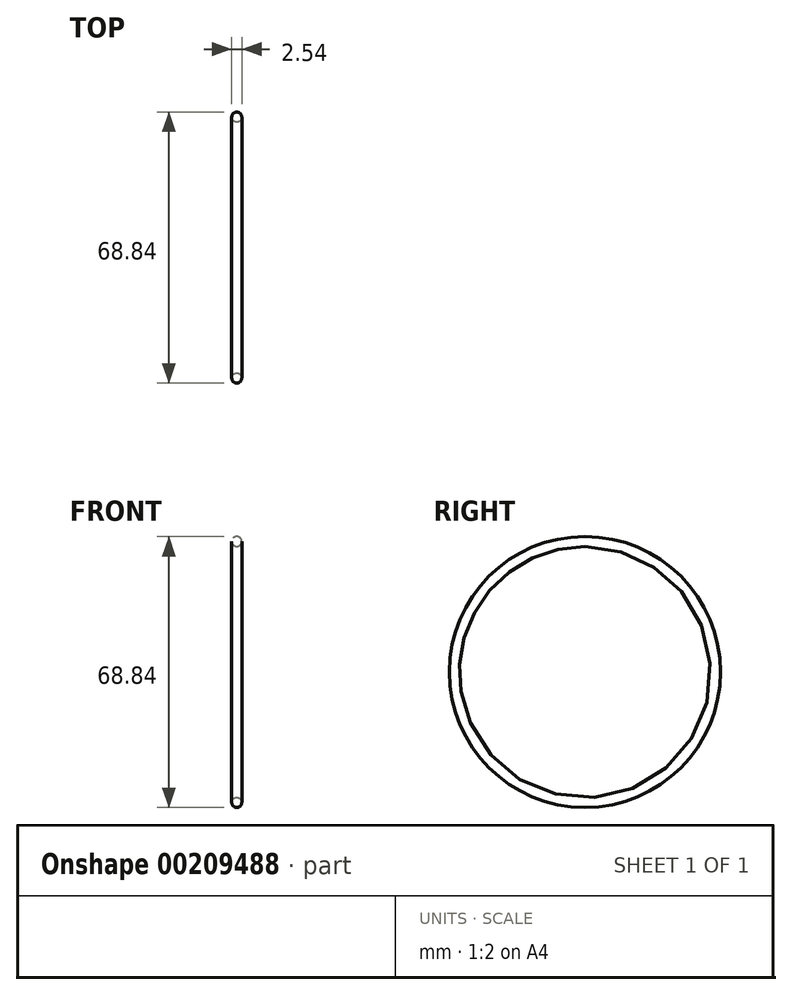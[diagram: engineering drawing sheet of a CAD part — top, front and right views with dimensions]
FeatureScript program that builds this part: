
annotation { "Feature Type Name" : "Feature", "Feature Type Description" : "" }
export const myFeature = defineFeature(function(context is Context, id is Id, definition is map)
    precondition{}
    {
        {
            var Q0;
            Q0=qCreatedBy(makeId("Front.planeOp"),FACE);
            var sketch = newSketch(context, id + "F0", { "sketchPlane" : qUnion([Q0])});
            skCircle(sketch, "E0", {"center": v(0, 33.15) * mm, "radius": 1.27 * mm});
            skLineSegment(sketch, "E1", {"start": v(-11.38, 0) * mm, "end": v(23.45, 0) * mm});
            skSolve(sketch);
        }
        {
            var Q0;
            Q0 = qSketchRegion(id + "F0", true);
            var Q1;
            Q1=sQuery(id+"F0.wireOp",EDGE,"E1");
            revolve(context, id + "F1", {"entities" : qUnion([Q0]), "axis" : qUnion([Q1]), "revolveType" : RevolveType.FULL});
        }
    });
